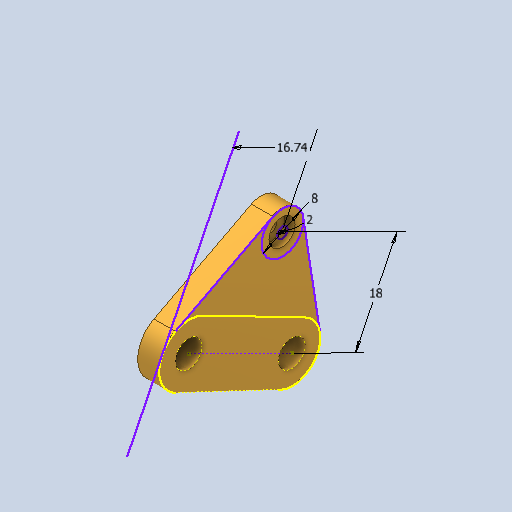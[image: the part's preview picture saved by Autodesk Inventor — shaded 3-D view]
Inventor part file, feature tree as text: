
AUTODESK INVENTOR PART (.ipt)
format: ipt  version: 2023 (Build 270158000, 158)  size: 155,648 bytes
history: native  units: in
note: dims shown in document units (in); Inventor stores cm internally (conversion verified against a paired STEP export)
features: extrude x3, sketch x3, projected_geometry x1
ambient origin geometry x8: Origin, YZ Plane, XZ Plane, XY Plane, X Axis, Y Axis, Z Axis, Center Point
bodies: Solid1 (feature_tree)
feature tree (7):
  extrude  "Extrusion1"  Depth=0.4523in
  extrude  "Extrusion2"  Depth=0.2118in
  extrude  "Extrusion3"  Depth=0.1575in TaperAngle=0.0deg
  sketch  "Sketch1"  dims[d0=0.2008in d1=0.2008in d3=0.4523in]
  sketch  "Sketch2"  dims[d4=0.2118in d5=0.8586in]
  projected_geometry  "Projected Loop1"
  sketch  "Sketch3"  dims[d6=0.8656in d7=0.1575in d8=0.0in d11=0.0787in d12=0.315in d13=0.1575in d14=0.0in d15=0.1969in d16=0.0787in d17=0.0in d18=0.6591in d19=0.7087in]
